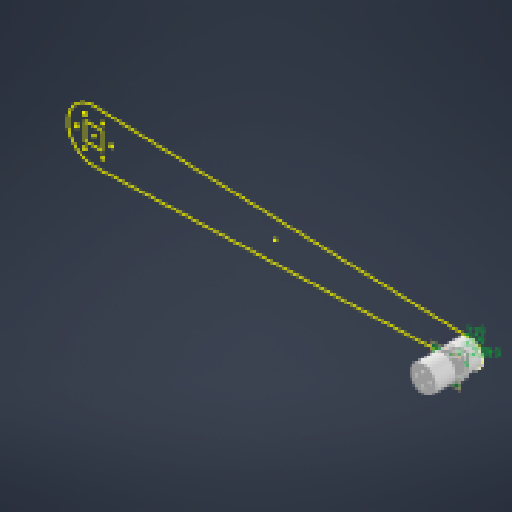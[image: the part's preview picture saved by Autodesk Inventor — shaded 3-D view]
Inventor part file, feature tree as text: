
AUTODESK INVENTOR PART (.ipt)
format: ipt  version: 2024.1 (Build 281209000, 209)  size: 269,824 bytes
history: native  units: in
note: dims shown in document units (in); Inventor stores cm internally (conversion verified against a paired STEP export)
features: extrude x6, sketch x3, plane x3, other x3, fillet x2, mirror x1, chamfer x1, reference x1
ambient origin geometry x8: Origin, YZ Plane, XZ Plane, XY Plane, X Axis, Y Axis, Z Axis, Center Point
bodies: Solid1 (feature_tree)
feature tree (20):
  sketch  "Sketch1"  dims[d0=0.219in d1=0.219in]
  extrude  "Extrusion1"  Depth=0.219in
  extrude  "Extrusion3"  Depth=0.219in
  plane  "Work Plane1"
  mirror  "Mirror1"
  plane  "Work Plane4"
  sketch  "Sketch4"  dims[d4=2.6496in d5=0.0in d8=0.75in d9=0.0in d14=11.2018in d15=0.5in d16=0.5in d17=0.3in d18=0.3in d19=0.0in d20=0.0in d21=0.2in d22=0.0in d23=0.15in d24=0.125in d25=45.0deg d26=0.15in d27=0.1181in d28=0.1575in d29=0.9in d30=0.75in d31=30.0deg d32=0.75in d33=1.0in d34=0.3779in d35=1.0in d36=0.3779in d37=0.1772in d38=0.1772in d39=0.5in d40=0.5in d41=0.5in d42=0.4in d43=0.0in d44=0.25in d45=0.0in d46=0.125in d47=0.125in]
  extrude  "Extrusion6"  Depth=0.75in TaperAngle=0.0deg
  extrude  "Extrusion7"  Depth=11.2018in
  fillet  "Fillet1"  Radius=0.5in
  fillet  "Fillet2"  Radius=0.5in
  plane  "Work Plane3"
  sketch  "Sketch3"  dims[d2=0.219in d3=0.219in]
  extrude  "Extrusion4"  Depth=0.125in
  extrude  "Extrusion5"  Depth=0.125in
  chamfer  "Chamfer2"  [1 undecoded]
  reference  "Reference1"
  other  "<userpath>\Documents\School\FallCAD\Trebuchet\Trebuchet.iam"
  other  "Trebuchet.iam"
  other  "MainArm:2"
note: 1 required parameter value undecoded (feature->parameter linkage not recoverable at this tier; creation-order binding heuristic only, values carry confidence <= 0.55)
